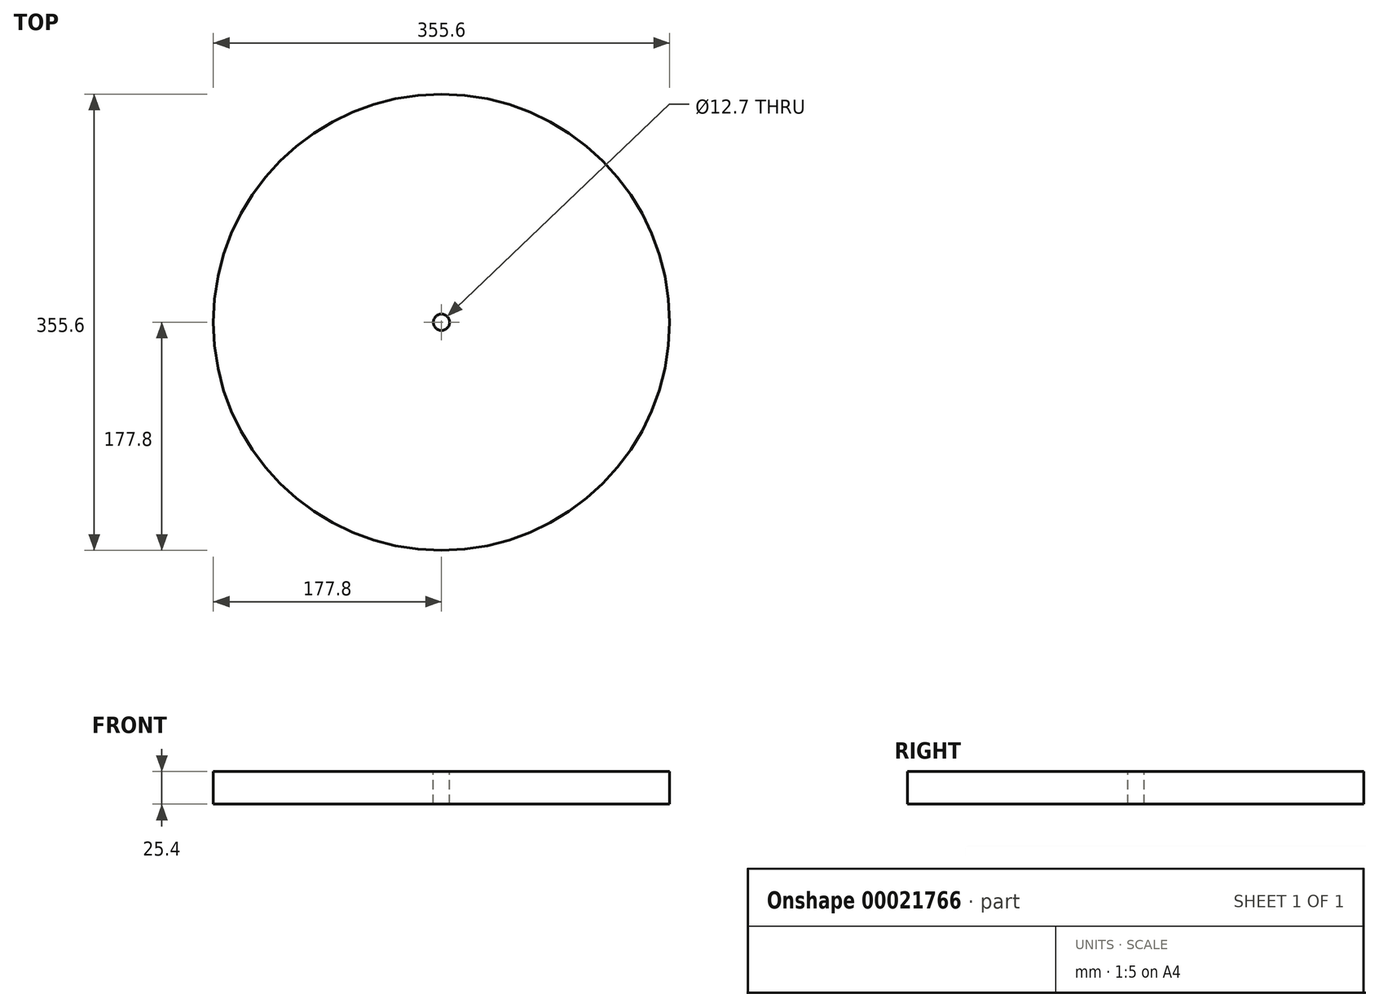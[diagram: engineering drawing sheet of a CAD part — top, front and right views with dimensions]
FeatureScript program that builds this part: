
annotation { "Feature Type Name" : "Feature", "Feature Type Description" : "" }
export const myFeature = defineFeature(function(context is Context, id is Id, definition is map)
    precondition{}
    {
        {
            var Q0;
            Q0=qCreatedBy(makeId("Top.planeOp"),FACE);
            var sketch = newSketch(context, id + "F0", { "sketchPlane" : qUnion([Q0])});
            skCircle(sketch, "E0", {"center": v(0, 0) * mm, "radius": 177.8 * mm});
            skSolve(sketch);
        }
        {
            var Q0;
            Q0=makeQuery(id+"F0.imprint","IMPRINT",FACE,{"disambiguationData":[TD([[makeQuery(id+"F0.imprint","IMPRINT",EDGE,{"derivedFrom":sQuery(id+"F0.wireOp",EDGE,"E0")}),1.0]])]});
            extrude(context, id + "F1", {"entities" : qUnion([Q0]), "depth" : 25.4 * mm});
        }
        {
            var Q0;
            Q0=makeQuery(id+"F1.opExtrude","CAP_FACE",FACE,{"disambiguationData":[OSD([sQuery(id+"F0.wireOp",EDGE,"E0")])],"isStart":false});
            var sketch = newSketch(context, id + "F2", { "sketchPlane" : qUnion([Q0])});
            skCircle(sketch, "E1", {"center": v(0, 0) * mm, "radius": 6.35 * mm});
            skSolve(sketch);
        }
        {
            var Q0;
            Q0=makeQuery(id+"F2.imprint","IMPRINT",FACE,{"disambiguationData":[TD([[makeQuery(id+"F2.imprint","IMPRINT",EDGE,{"derivedFrom":sQuery(id+"F2.wireOp",EDGE,"E1")}),-1.0]])]});
            var sketch = newSketch(context, id + "F3", { "sketchPlane" : qUnion([Q0])});
            skLineSegment(sketch, "E2", {"start": v(-88.9, 0) * mm, "end": v(0, 0) * mm});
            skLineSegment(sketch, "E3", {"start": v(0, 0) * mm, "end": v(88.9, 0) * mm});
            skPoint(sketch, "E4", {"position": v(-88.9, 0) * mm});
            skPoint(sketch, "E5", {"position": v(88.9, 0) * mm});
            skSolve(sketch);
        }
        {
            var Q0;
            Q0=sQuery(id+"F3.wireOp",VERTEX,"E3.start");
            var Q1;
            Q1=makeQuery(id+"F1.opExtrude","SWEPT_BODY",BODY,{"disambiguationData":[OSD([sQuery(id+"F0.wireOp",EDGE,"E0")])]});
            hole(context, id + "F4", {"style" : HoleStyle.SIMPLE, "holeDiameter" : 12.7 * mm, "endStyle" : HoleEndStyle.THROUGH, "locations" : qUnion([Q0]), "scope" : qUnion([Q1])});
        }
    });
